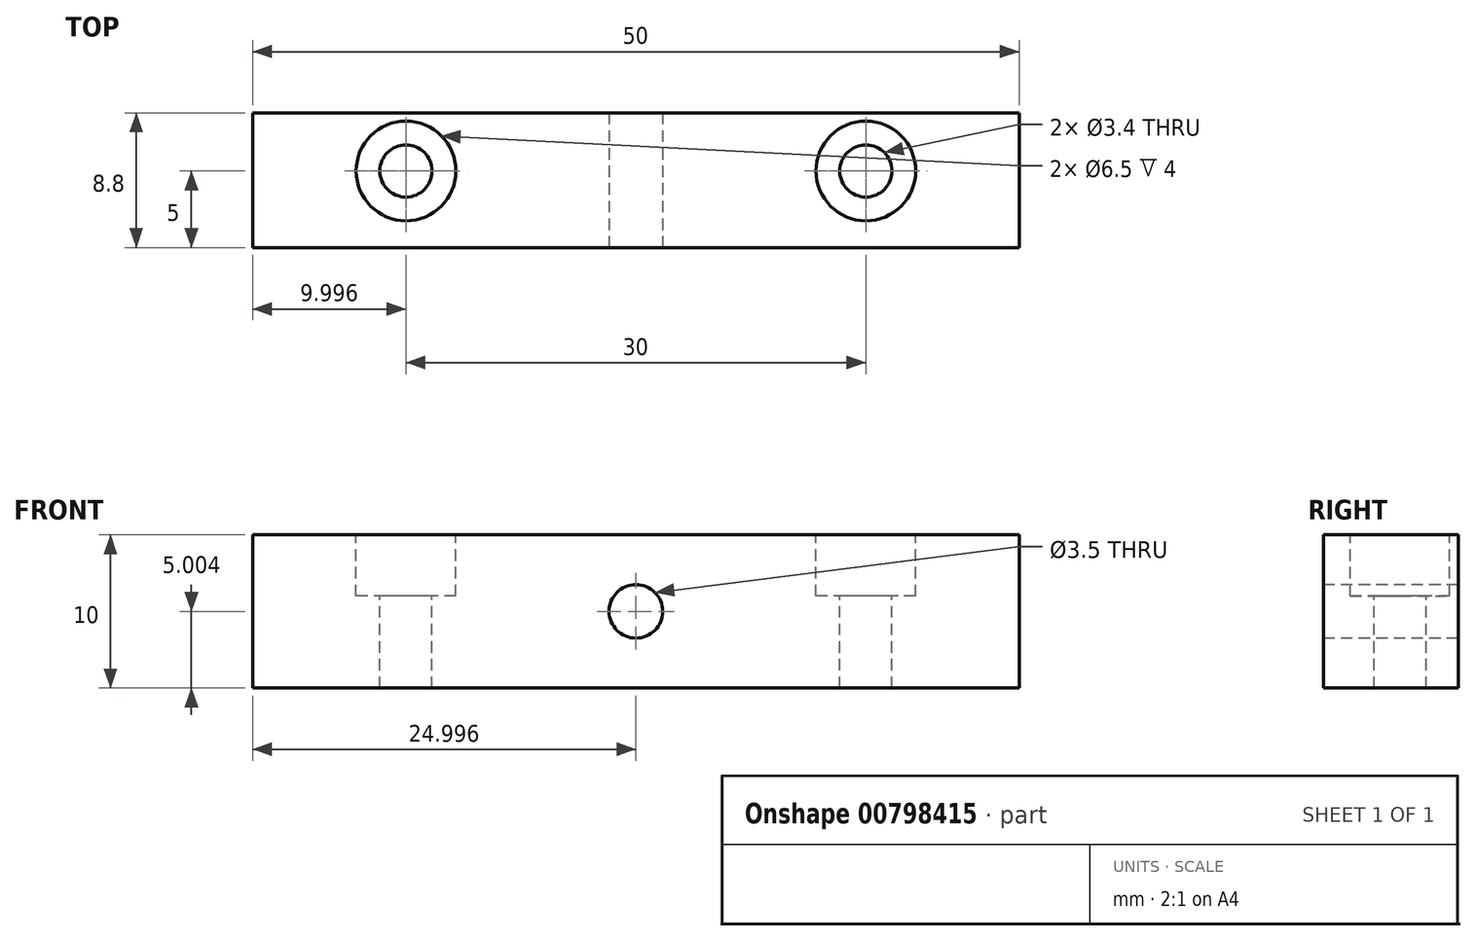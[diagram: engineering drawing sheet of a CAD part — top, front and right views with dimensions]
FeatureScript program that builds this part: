
annotation { "Feature Type Name" : "Feature", "Feature Type Description" : "" }
export const myFeature = defineFeature(function(context is Context, id is Id, definition is map)
    precondition{}
    {
        {
            var Q0;
            Q0=qCreatedBy(makeId("Front.planeOp"),FACE);
            var sketch = newSketch(context, id + "F0", { "sketchPlane" : qUnion([Q0])});
            skLineSegment(sketch, "E0.bottom", {"start": v(-38, 4.07) * mm, "end": v(12, 4.07) * mm});
            skLineSegment(sketch, "E0.top", {"start": v(-38, -5.93) * mm, "end": v(12, -5.93) * mm});
            skLineSegment(sketch, "E0.left", {"start": v(-38, 4.07) * mm, "end": v(-38, -5.93) * mm});
            skLineSegment(sketch, "E0.right", {"start": v(12, 4.07) * mm, "end": v(12, -5.93) * mm});
            skSolve(sketch);
        }
        {
            var Q0;
            Q0=makeQuery(id+"F0.imprint","IMPRINT",FACE,{"disambiguationData":[TD([[makeQuery(id+"F0.imprint","IMPRINT",EDGE,{"derivedFrom":sQuery(id+"F0.wireOp",EDGE,"E0.bottom")}),-1.0]])]});
            extrude(context, id + "F1", {"entities" : qUnion([Q0]), "depth" : 10 * mm, "offsetDistance" : 25 * mm});
        }
        {
            var Q0;
            Q0=makeQuery(id+"F1.opExtrude","SWEPT_FACE",FACE,{"disambiguationData":[OSD([sQuery(id+"F0.wireOp",EDGE,"E0.bottom")])]});
            var sketch = newSketch(context, id + "F2", { "sketchPlane" : qUnion([Q0])});
            skLineSegment(sketch, "E1", {"start": v(-38, -5) * mm, "end": v(12, -5) * mm, "construction": true});
            skLineSegment(sketch, "E2", {"start": v(-13, 0) * mm, "end": v(-13, -10) * mm, "construction": true});
            skLineSegment(sketch, "E3", {"start": v(-28, 0) * mm, "end": v(-28, -10) * mm, "construction": true});
            skLineSegment(sketch, "E4", {"start": v(2, 0) * mm, "end": v(2, -10) * mm, "construction": true});
            skPoint(sketch, "E5", {"position": v(-28, -5) * mm});
            skPoint(sketch, "E6", {"position": v(2, -5) * mm});
            skSolve(sketch);
        }
        {
            var Q0;
            Q0=sQuery(id+"F2.wireOp",VERTEX,"E5");
            var Q1;
            Q1=sQuery(id+"F2.wireOp",VERTEX,"E6");
            var Q2;
            Q2=makeQuery(id+"F1.opExtrude","SWEPT_BODY",BODY,{"disambiguationData":[OSD([sQuery(id+"F0.wireOp",EDGE,"E0.bottom"),sQuery(id+"F0.wireOp",EDGE,"E0.top"),sQuery(id+"F0.wireOp",EDGE,"E0.left"),sQuery(id+"F0.wireOp",EDGE,"E0.right")])]});
            hole(context, id + "F3", {"style" : HoleStyle.C_BORE, "endStyle" : HoleEndStyle.THROUGH, "holeDiameter" : 3.4 * mm, "cBoreDiameter" : 6.5 * mm, "cBoreDepth" : 4 * mm, "majorDiameter" : 5 * mm, "isTappedThrough" : true, "tappedDepth" : 12 * mm, "tapClearance" : 3, "locations" : qUnion([Q0, Q1]), "scope" : qUnion([Q2])});
        }
        {
            var Q0;
            Q0=makeQuery(id+"F1.opExtrude","CAP_FACE",FACE,{"disambiguationData":[OSD([sQuery(id+"F0.wireOp",EDGE,"E0.bottom"),sQuery(id+"F0.wireOp",EDGE,"E0.top"),sQuery(id+"F0.wireOp",EDGE,"E0.left"),sQuery(id+"F0.wireOp",EDGE,"E0.right")])],"isStart":false});
            var sketch = newSketch(context, id + "F4", { "sketchPlane" : qUnion([Q0])});
            skLineSegment(sketch, "E7", {"start": v(-38, -0.93) * mm, "end": v(12, -0.93) * mm, "construction": true});
            skLineSegment(sketch, "E8", {"start": v(-13, 4.07) * mm, "end": v(-13, -5.93) * mm, "construction": true});
            skPoint(sketch, "E9", {"position": v(-13, -0.93) * mm});
            skSolve(sketch);
        }
        {
            var Q0;
            Q0=sQuery(id+"F4.wireOp",VERTEX,"E9");
            var Q1;
            Q1=makeQuery(id+"F1.opExtrude","SWEPT_BODY",BODY,{"disambiguationData":[OSD([sQuery(id+"F0.wireOp",EDGE,"E0.bottom"),sQuery(id+"F0.wireOp",EDGE,"E0.top"),sQuery(id+"F0.wireOp",EDGE,"E0.left"),sQuery(id+"F0.wireOp",EDGE,"E0.right")])]});
            hole(context, id + "F5", {"style" : HoleStyle.SIMPLE, "endStyle" : HoleEndStyle.THROUGH, "standardTappedOrClearance" : lookupTablePath({ "standard" : "ISO", "engagement" : "75%", "pitch" : "0.5 mm", "size" : "M4", "type" : "Tapped" }), "standardBlindInLast" : lookupTablePath({ "standard" : "ISO", "fit" : "Normal", "engagement" : "75%", "pitch" : "0.5 mm", "size" : "M4", "type" : "Clearance & tapped" }), "holeDiameter" : 3.5 * mm, "majorDiameter" : 4 * mm, "showTappedDepth" : true, "isTappedThrough" : true, "tappedDepth" : 12 * mm, "tapClearance" : 3, "locations" : qUnion([Q0]), "scope" : qUnion([Q1])});
        }
        {
            var Q0;
            Q0=makeQuery(id+"F1.opExtrude","CAP_FACE",FACE,{"disambiguationData":[OSD([sQuery(id+"F0.wireOp",EDGE,"E0.bottom"),sQuery(id+"F0.wireOp",EDGE,"E0.top"),sQuery(id+"F0.wireOp",EDGE,"E0.left"),sQuery(id+"F0.wireOp",EDGE,"E0.right")])],"isStart":true});
            extrude(context, id + "F6", {"entities" : qUnion([Q0]), "operationType" : NewBodyOperationType.REMOVE, "oppositeDirection" : true, "depth" : 1.2 * mm, "offsetDistance" : 25 * mm});
        }
    });
